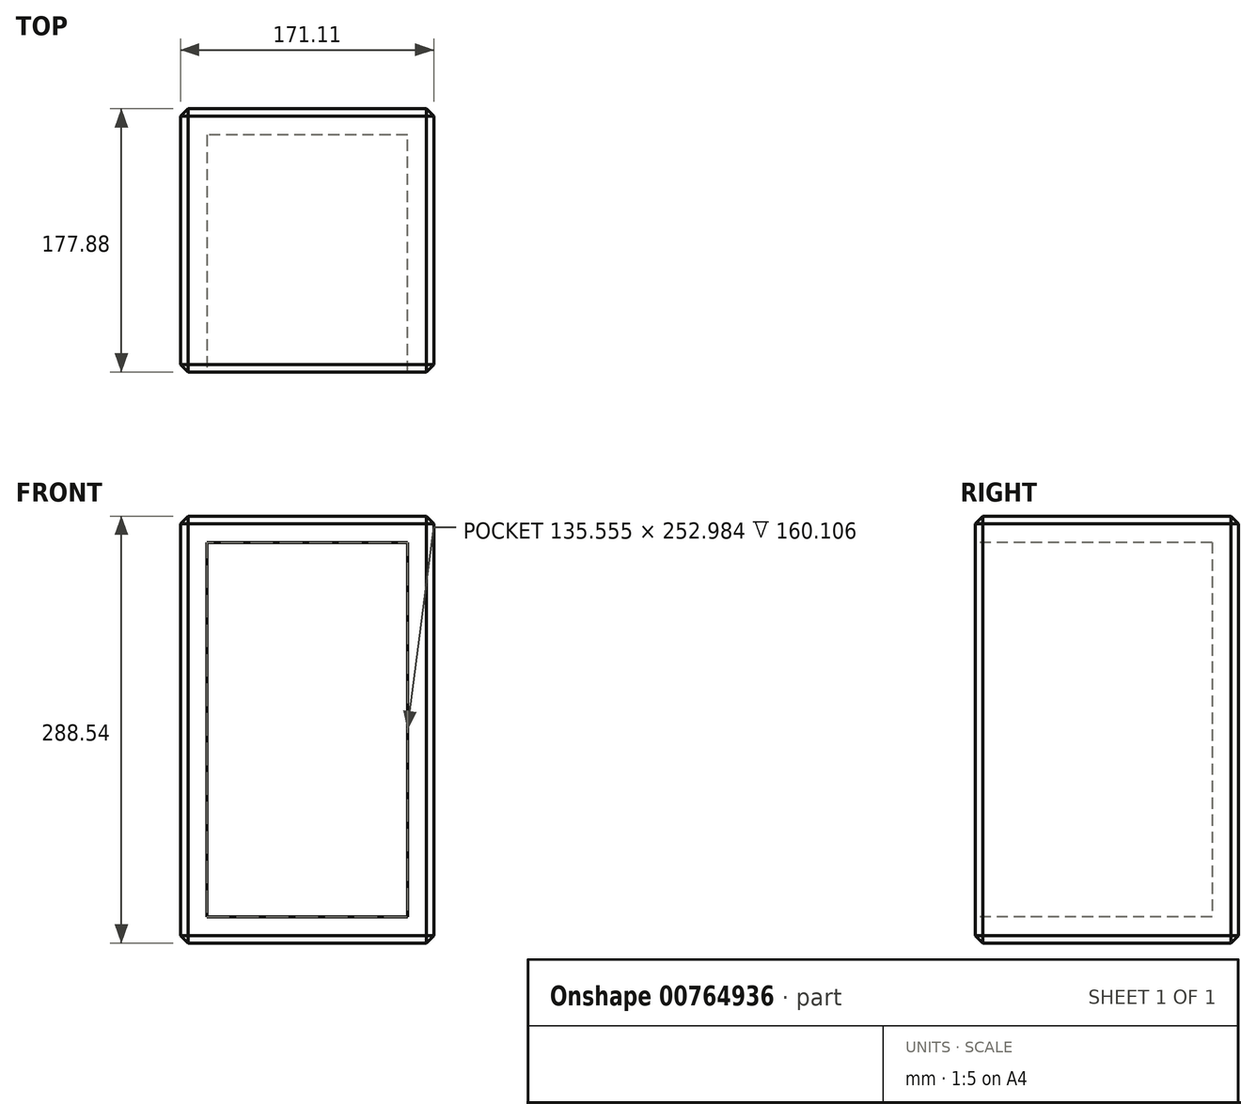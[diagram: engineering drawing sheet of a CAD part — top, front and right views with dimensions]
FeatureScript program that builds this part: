
annotation { "Feature Type Name" : "Feature", "Feature Type Description" : "" }
export const myFeature = defineFeature(function(context is Context, id is Id, definition is map)
    precondition{}
    {
        {
            var Q0;
            Q0=qCreatedBy(makeId("Top.planeOp"),FACE);
            var sketch = newSketch(context, id + "F0", { "sketchPlane" : qUnion([Q0])});
            skLineSegment(sketch, "E0", {"start": v(-94.36, 77.11) * mm, "end": v(-94.36, -100.77) * mm});
            skLineSegment(sketch, "E1", {"start": v(-94.36, -100.77) * mm, "end": v(76.75, -100.77) * mm});
            skLineSegment(sketch, "E2", {"start": v(76.75, -100.77) * mm, "end": v(76.75, 77.11) * mm});
            skLineSegment(sketch, "E3", {"start": v(76.75, 77.11) * mm, "end": v(-94.36, 77.11) * mm});
            skSolve(sketch);
        }
        {
            var Q0;
            Q0 = qSketchRegion(id + "F0", true);
            extrude(context, id + "F1", {"entities" : qUnion([Q0]), "depth" : 288.54 * mm, "offsetDistance" : 25.4 * mm});
        }
        {
            var Q0;
            Q0=makeQuery(id+"F1.opExtrude","SWEPT_FACE",FACE,{"disambiguationData":[OSD([sQuery(id+"F0.wireOp",EDGE,"E1")])]});
            shell(context, id + "F2", {"entities" : qUnion([Q0]), "thickness" : 17.78 * mm});
        }
        {
            var Q0;
            Q0=makeQuery(id+"F1.opExtrude","CAP_EDGE",EDGE,{"disambiguationData":[OSD([sQuery(id+"F0.wireOp",EDGE,"E1")])],"isStart":false});
            var Q1;
            Q1=makeQuery(id+"F1.opExtrude","CAP_EDGE",EDGE,{"disambiguationData":[OSD([sQuery(id+"F0.wireOp",EDGE,"E2")])],"isStart":false});
            var Q2;
            Q2=makeQuery(id+"F1.opExtrude","CAP_EDGE",EDGE,{"disambiguationData":[OSD([sQuery(id+"F0.wireOp",EDGE,"E3")])],"isStart":false});
            var Q3;
            Q3=makeQuery(id+"F1.opExtrude","CAP_EDGE",EDGE,{"disambiguationData":[OSD([sQuery(id+"F0.wireOp",EDGE,"E0")])],"isStart":false});
            var Q4;
            Q4=makeQuery(id+"F1.opExtrude","SWEPT_EDGE",EDGE,{"disambiguationData":[OSD([sQuery(id+"F0.wireOp",EDGE,"E0"),sQuery(id+"F0.wireOp",EDGE,"E3")])]});
            var Q5;
            Q5=makeQuery(id+"F1.opExtrude","SWEPT_EDGE",EDGE,{"disambiguationData":[OSD([sQuery(id+"F0.wireOp",EDGE,"E2"),sQuery(id+"F0.wireOp",EDGE,"E3")])]});
            var Q6;
            Q6=makeQuery(id+"F1.opExtrude","SWEPT_EDGE",EDGE,{"disambiguationData":[OSD([sQuery(id+"F0.wireOp",EDGE,"E1"),sQuery(id+"F0.wireOp",EDGE,"E2")])]});
            var Q7;
            Q7=makeQuery(id+"F1.opExtrude","SWEPT_EDGE",EDGE,{"disambiguationData":[OSD([sQuery(id+"F0.wireOp",EDGE,"E0"),sQuery(id+"F0.wireOp",EDGE,"E1")])]});
            var Q8;
            Q8=makeQuery(id+"F1.opExtrude","CAP_EDGE",EDGE,{"disambiguationData":[OSD([sQuery(id+"F0.wireOp",EDGE,"E0")])],"isStart":true});
            var Q9;
            Q9=makeQuery(id+"F1.opExtrude","CAP_EDGE",EDGE,{"disambiguationData":[OSD([sQuery(id+"F0.wireOp",EDGE,"E1")])],"isStart":true});
            var Q10;
            Q10=makeQuery(id+"F1.opExtrude","CAP_EDGE",EDGE,{"disambiguationData":[OSD([sQuery(id+"F0.wireOp",EDGE,"E2")])],"isStart":true});
            var Q11;
            Q11=makeQuery(id+"F1.opExtrude","CAP_EDGE",EDGE,{"disambiguationData":[OSD([sQuery(id+"F0.wireOp",EDGE,"E3")])],"isStart":true});
            chamfer(context, id + "F3", {"entities" : qUnion([Q0, Q1, Q2, Q3, Q4, Q5, Q6, Q7, Q8, Q9, Q10, Q11]), "width" : 5.08 * mm, "tangentPropagation" : true});
        }
    });
